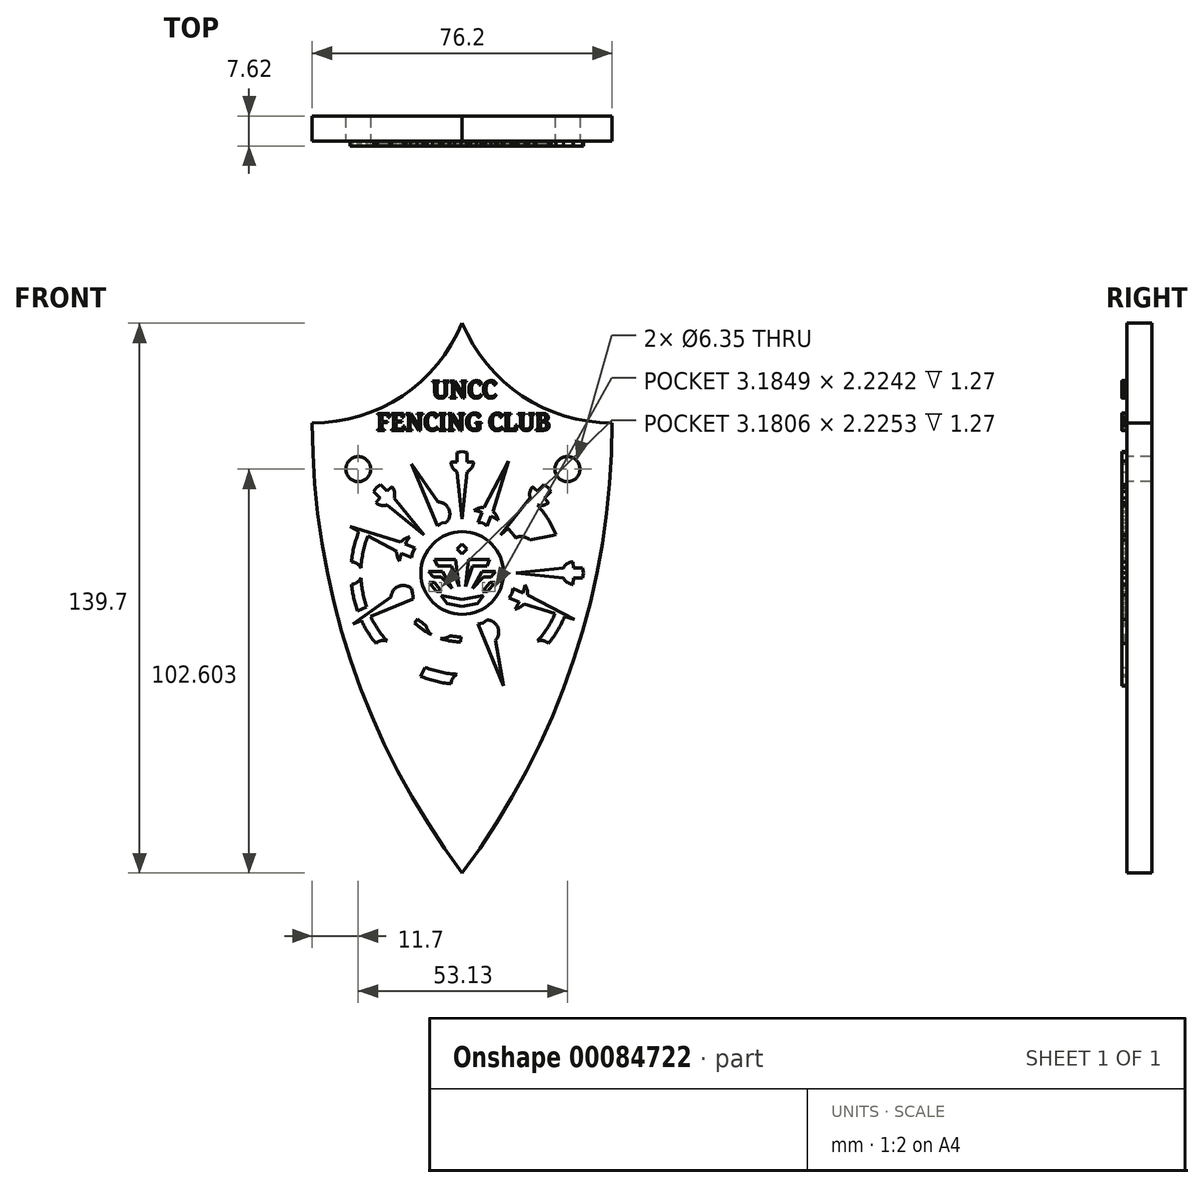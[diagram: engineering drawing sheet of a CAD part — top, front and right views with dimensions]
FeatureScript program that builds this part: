
annotation { "Feature Type Name" : "Feature", "Feature Type Description" : "" }
export const myFeature = defineFeature(function(context is Context, id is Id, definition is map)
    precondition{}
    {
        {
            var Q0;
            Q0=qCreatedBy(makeId("Front.planeOp"),FACE);
            var sketch = newSketch(context, id + "F0", { "sketchPlane" : qUnion([Q0])});
            skLineSegment(sketch, "E0", {"start": v(0, 0) * mm, "end": v(0, 38.1) * mm});
            skLineSegment(sketch, "E1", {"start": v(0, 38.1) * mm, "end": v(-38.1, 38.1) * mm});
            skLineSegment(sketch, "E2", {"start": v(0, 38.1) * mm, "end": v(0, 63.5) * mm});
            skLineSegment(sketch, "E3", {"start": v(0, 0) * mm, "end": v(0, -76.2) * mm});
            skArc(sketch, "E4", {"start": v(-38.1, 38.1) * mm, "mid": v(-28.32, -22.14) * mm, "end": v(0, -76.2) * mm});
            skArc(sketch, "E5", {"start": v(-38.1, 38.1) * mm, "mid": v(-15.2, 45.03) * mm, "end": v(0, 63.5) * mm});
            skArc(sketch, "E6.MirrorCS", {"start": v(38.1, 38.1) * mm, "mid": v(28.32, -22.14) * mm, "end": v(0, -76.2) * mm});
            skLineSegment(sketch, "E7.MirrorCS", {"start": v(0, 38.1) * mm, "end": v(38.1, 38.1) * mm});
            skArc(sketch, "E8.MirrorCS", {"start": v(38.1, 38.1) * mm, "mid": v(15.2, 45.03) * mm, "end": v(0, 63.5) * mm});
            skSolve(sketch);
        }
        {
            var Q0;
            Q0=makeQuery(id+"F0.imprint","IMPRINT",FACE,{"disambiguationData":[TD([[makeQuery(id+"F0.imprint","IMPRINT",EDGE,{"derivedFrom":sQuery(id+"F0.wireOp",EDGE,"E1")}),-1.0]])]});
            var Q1;
            Q1=makeQuery(id+"F0.imprint","IMPRINT",FACE,{"disambiguationData":[TD([[makeQuery(id+"F0.imprint","IMPRINT",EDGE,{"derivedFrom":sQuery(id+"F0.wireOp",EDGE,"E2")}),-1.0]])]});
            var Q2;
            Q2=makeQuery(id+"F0.imprint","IMPRINT",FACE,{"disambiguationData":[TD([[makeQuery(id+"F0.imprint","IMPRINT",EDGE,{"derivedFrom":sQuery(id+"F0.wireOp",EDGE,"E0")}),1.0]])]});
            var Q3;
            Q3=makeQuery(id+"F0.imprint","IMPRINT",FACE,{"disambiguationData":[TD([[makeQuery(id+"F0.imprint","IMPRINT",EDGE,{"derivedFrom":sQuery(id+"F0.wireOp",EDGE,"E0")}),-1.0]])]});
            extrude(context, id + "F1", {"entities" : qUnion([Q0, Q1, Q2, Q3]), "depth" : 6.35 * mm});
        }
        {
            var Q0;
            Q0=makeQuery(id+"F1.opExtrude","CAP_FACE",FACE,{"disambiguationData":[OSD([sQuery(id+"F0.wireOp",EDGE,"E4"),sQuery(id+"F0.wireOp",EDGE,"E5"),sQuery(id+"F0.wireOp",EDGE,"E6.MirrorCS"),sQuery(id+"F0.wireOp",EDGE,"E8.MirrorCS")])],"isStart":false});
            var sketch = newSketch(context, id + "F2", { "sketchPlane" : qUnion([Q0])});
            skCircle(sketch, "E9.cCircle", {"center": v(0, 0) * mm, "radius": 30.82 * mm, "construction": true});
            skLineSegment(sketch, "E9.0", {"start": v(30.82, 0) * mm, "end": v(28.48, -11.8) * mm});
            skLineSegment(sketch, "E9.1", {"start": v(28.48, -11.8) * mm, "end": v(21.8, -21.8) * mm});
            skLineSegment(sketch, "E9.2", {"start": v(21.8, -21.8) * mm, "end": v(11.8, -28.48) * mm});
            skLineSegment(sketch, "E9.3", {"start": v(11.8, -28.48) * mm, "end": v(0, -30.82) * mm});
            skLineSegment(sketch, "E9.4", {"start": v(0, -30.82) * mm, "end": v(-11.8, -28.48) * mm});
            skLineSegment(sketch, "E9.5", {"start": v(-11.8, -28.48) * mm, "end": v(-21.8, -21.8) * mm});
            skLineSegment(sketch, "E9.6", {"start": v(-21.8, -21.8) * mm, "end": v(-28.48, -11.8) * mm});
            skLineSegment(sketch, "E9.7", {"start": v(-28.48, -11.8) * mm, "end": v(-30.82, 0) * mm});
            skLineSegment(sketch, "E9.8", {"start": v(-30.82, 0) * mm, "end": v(-28.48, 11.8) * mm});
            skLineSegment(sketch, "E9.9", {"start": v(-28.48, 11.8) * mm, "end": v(-21.8, 21.8) * mm});
            skLineSegment(sketch, "E9.10", {"start": v(-21.8, 21.8) * mm, "end": v(-11.8, 28.48) * mm});
            skLineSegment(sketch, "E9.11", {"start": v(-11.8, 28.48) * mm, "end": v(0, 30.82) * mm});
            skLineSegment(sketch, "E9.12", {"start": v(0, 30.82) * mm, "end": v(11.8, 28.48) * mm});
            skLineSegment(sketch, "E9.13", {"start": v(11.8, 28.48) * mm, "end": v(21.8, 21.8) * mm});
            skLineSegment(sketch, "E9.14", {"start": v(21.8, 21.8) * mm, "end": v(28.48, 11.8) * mm});
            skLineSegment(sketch, "E9.15", {"start": v(28.48, 11.8) * mm, "end": v(30.82, 0) * mm});
            skCircle(sketch, "E10.cCircle", {"center": v(0, 0) * mm, "radius": 13.7 * mm, "construction": true});
            skLineSegment(sketch, "E10.0", {"start": v(13.7, 0) * mm, "end": v(12.66, -5.24) * mm});
            skLineSegment(sketch, "E10.1", {"start": v(12.66, -5.24) * mm, "end": v(9.69, -9.69) * mm});
            skLineSegment(sketch, "E10.2", {"start": v(9.69, -9.69) * mm, "end": v(5.24, -12.66) * mm});
            skLineSegment(sketch, "E10.3", {"start": v(5.24, -12.66) * mm, "end": v(0, -13.7) * mm});
            skLineSegment(sketch, "E10.4", {"start": v(0, -13.7) * mm, "end": v(-5.24, -12.66) * mm});
            skLineSegment(sketch, "E10.5", {"start": v(-5.24, -12.66) * mm, "end": v(-9.69, -9.69) * mm});
            skLineSegment(sketch, "E10.6", {"start": v(-9.69, -9.69) * mm, "end": v(-12.66, -5.24) * mm});
            skLineSegment(sketch, "E10.7", {"start": v(-12.66, -5.24) * mm, "end": v(-13.7, 0) * mm});
            skLineSegment(sketch, "E10.8", {"start": v(-13.7, 0) * mm, "end": v(-12.66, 5.24) * mm});
            skLineSegment(sketch, "E10.9", {"start": v(-12.66, 5.24) * mm, "end": v(-9.69, 9.69) * mm});
            skLineSegment(sketch, "E10.10", {"start": v(-9.69, 9.69) * mm, "end": v(-5.24, 12.66) * mm});
            skLineSegment(sketch, "E10.11", {"start": v(-5.24, 12.66) * mm, "end": v(0, 13.7) * mm});
            skLineSegment(sketch, "E10.12", {"start": v(0, 13.7) * mm, "end": v(5.24, 12.66) * mm});
            skLineSegment(sketch, "E10.13", {"start": v(5.24, 12.66) * mm, "end": v(9.69, 9.69) * mm});
            skLineSegment(sketch, "E10.14", {"start": v(9.69, 9.69) * mm, "end": v(12.66, 5.24) * mm});
            skLineSegment(sketch, "E10.15", {"start": v(12.66, 5.24) * mm, "end": v(13.7, 0) * mm});
            skLineSegment(sketch, "E11", {"start": v(-11.8, 28.48) * mm, "end": v(-9.5, 22.91) * mm});
            skLineSegment(sketch, "E12.MirrorCS", {"start": v(28.48, 11.8) * mm, "end": v(22.91, 9.5) * mm});
            skLineSegment(sketch, "E13.MirrorCS", {"start": v(-28.48, -11.8) * mm, "end": v(-22.91, -9.5) * mm});
            skLineSegment(sketch, "E14.MirrorCS", {"start": v(11.8, -28.48) * mm, "end": v(9.5, -22.91) * mm});
            skArc(sketch, "E15.0", {"start": v(-1.27, 25.71) * mm, "mid": v(-5.74, 25.1) * mm, "end": v(-10.04, 23.7) * mm});
            skArc(sketch, "E16.0", {"start": v(0, 17.5) * mm, "mid": v(-1.98, 17.4) * mm, "end": v(-3.94, 17.06) * mm});
            skArc(sketch, "E17.0", {"start": v(0, 16.24) * mm, "mid": v(-1.65, 16.16) * mm, "end": v(-3.28, 15.9) * mm});
            skArc(sketch, "E18.0", {"start": v(-1.27, 28.26) * mm, "mid": v(-6.51, 27.52) * mm, "end": v(-11.53, 25.83) * mm});
            skLineSegment(sketch, "E19.0", {"start": v(-1.27, 30.82) * mm, "end": v(-1.27, 28.26) * mm});
            skLineSegment(sketch, "E20.0", {"start": v(1.27, 30.82) * mm, "end": v(1.27, 28.26) * mm});
            skLineSegment(sketch, "E21", {"start": v(0, 13.7) * mm, "end": v(0.01, 25.74) * mm});
            skLineSegment(sketch, "E22.MirrorCS", {"start": v(0, -13.7) * mm, "end": v(-1.27, -25.71) * mm});
            skLineSegment(sketch, "E23.MirrorCS", {"start": v(0, -13.7) * mm, "end": v(1.27, -25.71) * mm});
            skArc(sketch, "E24.MirrorCS", {"start": v(-2.86, -28.14) * mm, "mid": v(-2.4, -26.7) * mm, "end": v(-1.27, -25.71) * mm});
            skArc(sketch, "E25.MirrorCS", {"start": v(1.27, -25.71) * mm, "mid": v(2.4, -26.7) * mm, "end": v(2.86, -28.14) * mm});
            skLineSegment(sketch, "E26.MirrorCS", {"start": v(1.27, -30.82) * mm, "end": v(1.27, -28.26) * mm});
            skLineSegment(sketch, "E27.MirrorCS", {"start": v(-1.27, -30.82) * mm, "end": v(-1.27, -28.26) * mm});
            skLineSegment(sketch, "E28.0", {"start": v(30.82, 1.27) * mm, "end": v(28.26, 1.27) * mm});
            skLineSegment(sketch, "E29.0", {"start": v(30.82, -1.27) * mm, "end": v(28.26, -1.27) * mm});
            skLineSegment(sketch, "E30", {"start": v(13.7, 0) * mm, "end": v(25.71, 1.27) * mm});
            skLineSegment(sketch, "E31", {"start": v(13.7, 0) * mm, "end": v(25.71, -1.27) * mm});
            skArc(sketch, "E32", {"start": v(28.14, 2.86) * mm, "mid": v(26.7, 2.4) * mm, "end": v(25.71, 1.27) * mm});
            skArc(sketch, "E33.trimOffspring", {"start": v(28.26, 1.27) * mm, "mid": v(27.74, 5.52) * mm, "end": v(26.6, 9.64) * mm});
            skArc(sketch, "E34.trimOffspring", {"start": v(25.71, 1.27) * mm, "mid": v(25.25, 5.02) * mm, "end": v(24.24, 8.67) * mm});
            skArc(sketch, "E35.trimOffspring", {"start": v(25.71, -1.27) * mm, "mid": v(26.7, -2.4) * mm, "end": v(28.14, -2.86) * mm});
            skArc(sketch, "E36.trimOffspring", {"start": v(16.24, 0.27) * mm, "mid": v(16.02, 2.67) * mm, "end": v(15.44, 5.02) * mm});
            skLineSegment(sketch, "E37.MirrorCS", {"start": v(-13.7, 0) * mm, "end": v(-25.71, 1.27) * mm});
            skLineSegment(sketch, "E38.MirrorCS", {"start": v(-13.7, 0) * mm, "end": v(-25.71, -1.27) * mm});
            skArc(sketch, "E39.MirrorCS", {"start": v(-28.14, 2.86) * mm, "mid": v(-26.7, 2.4) * mm, "end": v(-25.71, 1.27) * mm});
            skArc(sketch, "E40.MirrorCS", {"start": v(-25.71, -1.27) * mm, "mid": v(-26.7, -2.4) * mm, "end": v(-28.14, -2.86) * mm});
            skLineSegment(sketch, "E41.MirrorCS", {"start": v(-30.82, 1.27) * mm, "end": v(-28.26, 1.27) * mm});
            skLineSegment(sketch, "E42.MirrorCS", {"start": v(-30.82, -1.27) * mm, "end": v(-28.26, -1.27) * mm});
            skLineSegment(sketch, "E43.0", {"start": v(-22.7, 20.9) * mm, "end": v(-20.88, 19.08) * mm});
            skLineSegment(sketch, "E44.0", {"start": v(-20.9, 22.7) * mm, "end": v(-19.08, 20.88) * mm});
            skLineSegment(sketch, "E45.0", {"start": v(22.7, 20.9) * mm, "end": v(20.88, 19.08) * mm});
            skLineSegment(sketch, "E46.0", {"start": v(20.9, 22.7) * mm, "end": v(19.08, 20.88) * mm});
            skLineSegment(sketch, "E47", {"start": v(-19.08, 17.28) * mm, "end": v(-9.69, 9.69) * mm});
            skLineSegment(sketch, "E48", {"start": v(-9.69, 9.69) * mm, "end": v(-17.28, 19.08) * mm});
            skArc(sketch, "E49", {"start": v(-21.92, 17.87) * mm, "mid": v(-20.58, 17.2) * mm, "end": v(-19.08, 17.28) * mm});
            skLineSegment(sketch, "E50", {"start": v(17.28, 19.08) * mm, "end": v(9.69, 9.69) * mm});
            skLineSegment(sketch, "E51", {"start": v(9.69, 9.69) * mm, "end": v(19.08, 17.28) * mm});
            skArc(sketch, "E52", {"start": v(17.87, 21.92) * mm, "mid": v(17.2, 20.58) * mm, "end": v(17.28, 19.08) * mm});
            skArc(sketch, "E53.trimOffspring", {"start": v(-20.88, 19.08) * mm, "mid": v(-23.8, 15.28) * mm, "end": v(-26.04, 11.05) * mm});
            skArc(sketch, "E54.trimOffspring", {"start": v(19.08, 20.88) * mm, "mid": v(15.28, 23.8) * mm, "end": v(11.05, 26.04) * mm});
            skArc(sketch, "E55.trimOffspring", {"start": v(17.28, 19.08) * mm, "mid": v(13.97, 21.62) * mm, "end": v(10.3, 23.6) * mm});
            skArc(sketch, "E56.trimOffspring", {"start": v(19.08, 17.28) * mm, "mid": v(20.58, 17.2) * mm, "end": v(21.92, 17.87) * mm});
            skArc(sketch, "E57.trimOffspring", {"start": v(12.1, 12.66) * mm, "mid": v(10.09, 14.31) * mm, "end": v(7.86, 15.65) * mm});
            skArc(sketch, "E58.trimOffspring", {"start": v(-12.66, 12.1) * mm, "mid": v(-14.31, 10.09) * mm, "end": v(-15.65, 7.86) * mm});
            skArc(sketch, "E59.trimOffspring", {"start": v(-19.08, 17.28) * mm, "mid": v(-21.62, 13.97) * mm, "end": v(-23.6, 10.3) * mm});
            skArc(sketch, "E60.trimOffspring", {"start": v(-17.28, 19.08) * mm, "mid": v(-17.2, 20.58) * mm, "end": v(-17.87, 21.92) * mm});
            skArc(sketch, "E61.trimOffspring", {"start": v(-11.67, 11.3) * mm, "mid": v(-13.22, 9.43) * mm, "end": v(-14.47, 7.37) * mm});
            skArc(sketch, "E62.trimOffspring", {"start": v(11.3, 11.67) * mm, "mid": v(9.43, 13.22) * mm, "end": v(7.37, 14.47) * mm});
            skPoint(sketch, "E63.orphan", {"position": v(0, -30.82) * mm});
            skArc(sketch, "E64.trimOffspring", {"start": v(1.27, -28.26) * mm, "mid": v(5.52, -27.74) * mm, "end": v(9.64, -26.6) * mm});
            skArc(sketch, "E65.trimOffspring", {"start": v(1.27, -25.71) * mm, "mid": v(5.02, -25.25) * mm, "end": v(8.67, -24.24) * mm});
            skArc(sketch, "E66.trimOffspring", {"start": v(0.4, -17.5) * mm, "mid": v(2.99, -17.25) * mm, "end": v(5.5, -16.62) * mm});
            skArc(sketch, "E67.trimOffspring", {"start": v(0.27, -16.24) * mm, "mid": v(2.67, -16.02) * mm, "end": v(5.02, -15.44) * mm});
            skLineSegment(sketch, "E68.MirrorCS", {"start": v(-9.69, -9.69) * mm, "end": v(-17.28, -19.08) * mm});
            skLineSegment(sketch, "E69.MirrorCS", {"start": v(-19.08, -17.28) * mm, "end": v(-9.69, -9.69) * mm});
            skArc(sketch, "E70.MirrorCS", {"start": v(-21.92, -17.87) * mm, "mid": v(-20.58, -17.2) * mm, "end": v(-19.08, -17.28) * mm});
            skArc(sketch, "E71.MirrorCS", {"start": v(-17.28, -19.08) * mm, "mid": v(-17.2, -20.58) * mm, "end": v(-17.87, -21.92) * mm});
            skLineSegment(sketch, "E72.MirrorCS", {"start": v(-20.9, -22.7) * mm, "end": v(-19.08, -20.88) * mm});
            skLineSegment(sketch, "E73.MirrorCS", {"start": v(-22.7, -20.9) * mm, "end": v(-20.88, -19.08) * mm});
            skLineSegment(sketch, "E74.MirrorCS", {"start": v(17.28, -19.08) * mm, "end": v(9.69, -9.69) * mm});
            skLineSegment(sketch, "E75.MirrorCS", {"start": v(9.69, -9.69) * mm, "end": v(19.08, -17.28) * mm});
            skArc(sketch, "E76.MirrorCS", {"start": v(19.08, -17.28) * mm, "mid": v(20.58, -17.2) * mm, "end": v(21.92, -17.87) * mm});
            skArc(sketch, "E77.MirrorCS", {"start": v(17.87, -21.92) * mm, "mid": v(17.2, -20.58) * mm, "end": v(17.28, -19.08) * mm});
            skLineSegment(sketch, "E78.MirrorCS", {"start": v(20.9, -22.7) * mm, "end": v(19.08, -20.88) * mm});
            skLineSegment(sketch, "E79.MirrorCS", {"start": v(22.7, -20.9) * mm, "end": v(20.88, -19.08) * mm});
            skLineSegment(sketch, "E80", {"start": v(-28.48, 11.8) * mm, "end": v(-15.65, 7.86) * mm});
            skLineSegment(sketch, "E81", {"start": v(-28.48, 11.8) * mm, "end": v(-16.62, 5.5) * mm});
            skArc(sketch, "E82", {"start": v(-13.42, 9.14) * mm, "mid": v(-14.64, 8.68) * mm, "end": v(-15.65, 7.86) * mm});
            skArc(sketch, "E83.trimOffspring", {"start": v(-15.44, 5.02) * mm, "mid": v(-16.02, 2.67) * mm, "end": v(-16.24, 0.27) * mm});
            skArc(sketch, "E84.trimOffspring", {"start": v(-16.62, 5.5) * mm, "mid": v(-16.5, 4.21) * mm, "end": v(-15.95, 3.03) * mm});
            skArc(sketch, "E85.trimOffspring", {"start": v(-16.62, 5.5) * mm, "mid": v(-17.25, 2.99) * mm, "end": v(-17.5, 0.4) * mm});
            skLineSegment(sketch, "E86.trimOffspring", {"start": v(-14.47, 7.37) * mm, "end": v(-11.94, 6.32) * mm});
            skLineSegment(sketch, "E87.trimOffspring", {"start": v(-15.44, 5.02) * mm, "end": v(-12.9, 3.97) * mm});
            skLineSegment(sketch, "E88", {"start": v(5.5, 16.62) * mm, "end": v(11.8, 28.48) * mm});
            skLineSegment(sketch, "E89", {"start": v(11.8, 28.48) * mm, "end": v(7.86, 15.65) * mm});
            skArc(sketch, "E90.trimOffspring", {"start": v(9.14, 13.42) * mm, "mid": v(8.68, 14.64) * mm, "end": v(7.86, 15.65) * mm});
            skLineSegment(sketch, "E91.trimOffspring", {"start": v(5.02, 15.44) * mm, "end": v(3.97, 12.9) * mm});
            skArc(sketch, "E92.trimOffspring", {"start": v(5.02, 15.44) * mm, "mid": v(2.54, 16.04) * mm, "end": v(0, 16.24) * mm});
            skLineSegment(sketch, "E93.trimOffspring", {"start": v(7.37, 14.47) * mm, "end": v(6.32, 11.94) * mm});
            skArc(sketch, "E94.trimOffspring", {"start": v(5.5, 16.62) * mm, "mid": v(4.21, 16.5) * mm, "end": v(3.03, 15.95) * mm});
            skArc(sketch, "E95.trimOffspring", {"start": v(5.5, 16.62) * mm, "mid": v(2.8, 17.29) * mm, "end": v(0, 17.5) * mm});
            skArc(sketch, "E96.MirrorCS", {"start": v(-7.86, -15.65) * mm, "mid": v(-8.68, -14.64) * mm, "end": v(-9.14, -13.42) * mm});
            skArc(sketch, "E97.MirrorCS", {"start": v(-3.03, -15.95) * mm, "mid": v(-4.21, -16.5) * mm, "end": v(-5.5, -16.62) * mm});
            skLineSegment(sketch, "E98.MirrorCS", {"start": v(-7.86, -15.65) * mm, "end": v(-11.8, -28.48) * mm});
            skLineSegment(sketch, "E99.MirrorCS", {"start": v(-11.8, -28.48) * mm, "end": v(-5.5, -16.62) * mm});
            skLineSegment(sketch, "E100.MirrorCS", {"start": v(-7.37, -14.47) * mm, "end": v(-6.32, -11.94) * mm});
            skLineSegment(sketch, "E101.MirrorCS", {"start": v(-5.02, -15.44) * mm, "end": v(-3.97, -12.9) * mm});
            skArc(sketch, "E102.trimOffspring", {"start": v(-5.02, -15.44) * mm, "mid": v(-2.67, -16.02) * mm, "end": v(-0.27, -16.24) * mm});
            skArc(sketch, "E103.trimOffspring", {"start": v(-5.5, -16.62) * mm, "mid": v(-2.99, -17.25) * mm, "end": v(-0.4, -17.5) * mm});
            skArc(sketch, "E104.trimOffspring", {"start": v(16.62, -5.5) * mm, "mid": v(17.25, -2.99) * mm, "end": v(17.5, -0.4) * mm});
            skArc(sketch, "E105.trimOffspring", {"start": v(15.44, -5.02) * mm, "mid": v(16.02, -2.67) * mm, "end": v(16.24, -0.27) * mm});
            skArc(sketch, "E106.trimOffspring", {"start": v(-28.26, -1.27) * mm, "mid": v(-27.52, -6.51) * mm, "end": v(-25.83, -11.53) * mm});
            skArc(sketch, "E107.trimOffspring", {"start": v(-25.71, -1.27) * mm, "mid": v(-25.1, -5.74) * mm, "end": v(-23.7, -10.04) * mm});
            skArc(sketch, "E108.trimOffspring", {"start": v(-17.5, -0.4) * mm, "mid": v(-17.37, -2.18) * mm, "end": v(-17.06, -3.94) * mm});
            skArc(sketch, "E109.trimOffspring", {"start": v(-19.08, -20.88) * mm, "mid": v(-15.28, -23.8) * mm, "end": v(-11.05, -26.04) * mm});
            skArc(sketch, "E110.trimOffspring", {"start": v(-17.28, -19.08) * mm, "mid": v(-13.97, -21.62) * mm, "end": v(-10.3, -23.6) * mm});
            skArc(sketch, "E111.trimOffspring", {"start": v(-12.1, -12.66) * mm, "mid": v(-10.09, -14.31) * mm, "end": v(-7.86, -15.65) * mm});
            skArc(sketch, "E112.trimOffspring", {"start": v(11.67, -11.3) * mm, "mid": v(13.22, -9.43) * mm, "end": v(14.47, -7.37) * mm});
            skArc(sketch, "E113.trimOffspring", {"start": v(12.66, -12.1) * mm, "mid": v(14.31, -10.09) * mm, "end": v(15.65, -7.86) * mm});
            skArc(sketch, "E114.trimOffspring", {"start": v(19.08, -17.28) * mm, "mid": v(21.62, -13.97) * mm, "end": v(23.6, -10.3) * mm});
            skArc(sketch, "E115.trimOffspring", {"start": v(20.88, -19.08) * mm, "mid": v(23.8, -15.28) * mm, "end": v(26.04, -11.05) * mm});
            skArc(sketch, "E116.trimOffspring", {"start": v(9.4, 23.97) * mm, "mid": v(5.4, 25.17) * mm, "end": v(1.27, 25.71) * mm});
            skArc(sketch, "E117.trimOffspring", {"start": v(10.6, 26.22) * mm, "mid": v(6.02, 27.64) * mm, "end": v(1.27, 28.26) * mm});
            skArc(sketch, "E118.trimOffspring", {"start": v(-26.22, 10.6) * mm, "mid": v(-27.64, 6.02) * mm, "end": v(-28.26, 1.27) * mm});
            skArc(sketch, "E119.trimOffspring", {"start": v(-23.97, 9.4) * mm, "mid": v(-25.17, 5.4) * mm, "end": v(-25.71, 1.27) * mm});
            skArc(sketch, "E120.trimOffspring", {"start": v(-11.3, -11.67) * mm, "mid": v(-9.43, -13.22) * mm, "end": v(-7.37, -14.47) * mm});
            skArc(sketch, "E121.trimOffspring", {"start": v(-16.24, -0.27) * mm, "mid": v(-16.14, -1.78) * mm, "end": v(-15.9, -3.28) * mm});
            skArc(sketch, "E122.trimOffspring", {"start": v(26.22, -10.6) * mm, "mid": v(27.64, -6.02) * mm, "end": v(28.26, -1.27) * mm});
            skArc(sketch, "E123.trimOffspring", {"start": v(23.97, -9.4) * mm, "mid": v(25.17, -5.4) * mm, "end": v(25.71, -1.27) * mm});
            skArc(sketch, "E124.trimOffspring", {"start": v(-10.6, -26.22) * mm, "mid": v(-6.02, -27.64) * mm, "end": v(-1.27, -28.26) * mm});
            skArc(sketch, "E125.trimOffspring", {"start": v(-9.4, -23.97) * mm, "mid": v(-5.4, -25.17) * mm, "end": v(-1.27, -25.71) * mm});
            skPoint(sketch, "E126.endSnap1", {"position": v(-11.17, -7.46) * mm});
            skLineSegment(sketch, "E127", {"start": v(-5.24, -4.65) * mm, "end": v(-6.51, -4.65) * mm});
            skLineSegment(sketch, "E128", {"start": v(-6.51, -4.65) * mm, "end": v(-8.42, -2.42) * mm});
            skLineSegment(sketch, "E129", {"start": v(-7.08, -2.42) * mm, "end": v(-5.24, -4.65) * mm});
            skLineSegment(sketch, "E130", {"start": v(-2.6, -3.96) * mm, "end": v(-5.38, -1.02) * mm});
            skLineSegment(sketch, "E131", {"start": v(-5.38, -1.02) * mm, "end": v(-7.31, -1.02) * mm});
            skLineSegment(sketch, "E132", {"start": v(-7.31, -1.02) * mm, "end": v(-8.5, 0.44) * mm});
            skLineSegment(sketch, "E133", {"start": v(-8.5, 0.44) * mm, "end": v(-5.03, 0.44) * mm});
            skLineSegment(sketch, "E134", {"start": v(-5.03, 0.44) * mm, "end": v(-2.6, -3.96) * mm});
            skLineSegment(sketch, "E135", {"start": v(-0.82, -3.38) * mm, "end": v(-2.68, 1.76) * mm});
            skLineSegment(sketch, "E136", {"start": v(-2.68, 1.76) * mm, "end": v(-6.3, 1.76) * mm});
            skLineSegment(sketch, "E137", {"start": v(-6.3, 1.76) * mm, "end": v(-7.01, 3.5) * mm});
            skLineSegment(sketch, "E138", {"start": v(-7.01, 3.5) * mm, "end": v(-1.66, 3.5) * mm});
            skLineSegment(sketch, "E139", {"start": v(-1.66, 3.5) * mm, "end": v(-0.82, -3.38) * mm});
            skLineSegment(sketch, "E140", {"start": v(-8.42, -2.42) * mm, "end": v(-7.08, -2.42) * mm});
            skLineSegment(sketch, "E141", {"start": v(0, 7.36) * mm, "end": v(-1.27, 6.1) * mm});
            skLineSegment(sketch, "E142", {"start": v(-1.27, 6.1) * mm, "end": v(0, 4.82) * mm});
            skLineSegment(sketch, "E143", {"start": v(0, 4.82) * mm, "end": v(0, 7.36) * mm});
            skLineSegment(sketch, "E144", {"start": v(-5.42, -5.68) * mm, "end": v(-3.9, -7.76) * mm});
            skLineSegment(sketch, "E145", {"start": v(-3.9, -7.76) * mm, "end": v(0, -8.45) * mm});
            skLineSegment(sketch, "E146", {"start": v(0, -8.45) * mm, "end": v(0, -6.75) * mm});
            skLineSegment(sketch, "E147", {"start": v(0, -6.75) * mm, "end": v(-5.42, -5.68) * mm});
            skLineSegment(sketch, "E148.MirrorCS", {"start": v(5.38, -5.7) * mm, "end": v(3.85, -7.77) * mm});
            skLineSegment(sketch, "E149.MirrorCS", {"start": v(7.28, -1.03) * mm, "end": v(8.47, 0.42) * mm});
            skLineSegment(sketch, "E150.MirrorCS", {"start": v(8.47, 0.42) * mm, "end": v(5, 0.43) * mm});
            skLineSegment(sketch, "E151.MirrorCS", {"start": v(7.04, -2.44) * mm, "end": v(5.2, -4.66) * mm});
            skLineSegment(sketch, "E152.MirrorCS", {"start": v(2.56, -3.96) * mm, "end": v(5.35, -1.03) * mm});
            skLineSegment(sketch, "E153.MirrorCS", {"start": v(5, 0.43) * mm, "end": v(2.56, -3.96) * mm});
            skLineSegment(sketch, "E154.MirrorCS", {"start": v(-0.04, -6.75) * mm, "end": v(5.38, -5.7) * mm});
            skLineSegment(sketch, "E155.MirrorCS", {"start": v(7, 3.5) * mm, "end": v(1.64, 3.5) * mm});
            skLineSegment(sketch, "E156.MirrorCS", {"start": v(5.35, -1.03) * mm, "end": v(7.28, -1.03) * mm});
            skLineSegment(sketch, "E157.MirrorCS", {"start": v(1.26, 6.09) * mm, "end": v(-0.02, 4.82) * mm});
            skLineSegment(sketch, "E158.MirrorCS", {"start": v(1.64, 3.5) * mm, "end": v(0.79, -3.38) * mm});
            skLineSegment(sketch, "E159.MirrorCS", {"start": v(6.48, -4.66) * mm, "end": v(8.4, -2.44) * mm});
            skLineSegment(sketch, "E160.MirrorCS", {"start": v(0.79, -3.38) * mm, "end": v(2.66, 1.75) * mm});
            skLineSegment(sketch, "E161.MirrorCS", {"start": v(3.85, -7.77) * mm, "end": v(-0.04, -8.45) * mm});
            skLineSegment(sketch, "E162.MirrorCS", {"start": v(0, 7.36) * mm, "end": v(1.26, 6.09) * mm});
            skLineSegment(sketch, "E163.MirrorCS", {"start": v(-0.02, 4.82) * mm, "end": v(0, 7.36) * mm});
            skLineSegment(sketch, "E164.MirrorCS", {"start": v(5.2, -4.66) * mm, "end": v(6.48, -4.66) * mm});
            skLineSegment(sketch, "E165.MirrorCS", {"start": v(6.28, 1.75) * mm, "end": v(7, 3.5) * mm});
            skLineSegment(sketch, "E166.MirrorCS", {"start": v(2.66, 1.75) * mm, "end": v(6.28, 1.75) * mm});
            skLineSegment(sketch, "E167.MirrorCS", {"start": v(8.4, -2.44) * mm, "end": v(7.04, -2.44) * mm});
            skLineSegment(sketch, "E168.MirrorCS", {"start": v(-0.04, -8.45) * mm, "end": v(-0.04, -6.75) * mm});
            skCircle(sketch, "E169", {"center": v(0, 0) * mm, "radius": 10.5 * mm});
            skLineSegment(sketch, "E170", {"start": v(-11.8, -28.48) * mm, "end": v(-5.24, -12.66) * mm});
            skLineSegment(sketch, "E171.MirrorCS", {"start": v(14.47, -7.37) * mm, "end": v(11.94, -6.32) * mm});
            skLineSegment(sketch, "E172.MirrorCS", {"start": v(15.44, -5.02) * mm, "end": v(12.9, -3.97) * mm});
            skArc(sketch, "E173.MirrorCS", {"start": v(15.95, -3.03) * mm, "mid": v(16.5, -4.21) * mm, "end": v(16.62, -5.5) * mm});
            skArc(sketch, "E174.MirrorCS", {"start": v(15.65, -7.86) * mm, "mid": v(14.64, -8.68) * mm, "end": v(13.42, -9.14) * mm});
            skLineSegment(sketch, "E175.MirrorCS", {"start": v(28.48, -11.8) * mm, "end": v(15.65, -7.86) * mm});
            skLineSegment(sketch, "E176.MirrorCS", {"start": v(28.48, -11.8) * mm, "end": v(16.62, -5.5) * mm});
            skLineSegment(sketch, "E177", {"start": v(-30.82, 0) * mm, "end": v(-13.7, 0) * mm});
            skLineSegment(sketch, "E178.MirrorCS", {"start": v(0, 13.7) * mm, "end": v(-1.27, 25.71) * mm});
            skLineSegment(sketch, "E179.MirrorCS", {"start": v(0, 13.7) * mm, "end": v(1.27, 25.71) * mm});
            skArc(sketch, "E180", {"start": v(-2.86, 28.14) * mm, "mid": v(-2.4, 26.7) * mm, "end": v(-1.27, 25.71) * mm});
            skArc(sketch, "E181.trimOffspring", {"start": v(1.27, 25.71) * mm, "mid": v(2.4, 26.7) * mm, "end": v(2.86, 28.14) * mm});
            skLineSegment(sketch, "E182.0", {"start": v(12.97, -28) * mm, "end": v(8.46, -17.1) * mm});
            skLineSegment(sketch, "E183.0", {"start": v(10.62, -28.96) * mm, "end": v(3.97, -12.9) * mm});
            skLineSegment(sketch, "E184.0", {"start": v(-28, -12.97) * mm, "end": v(-11.94, -6.32) * mm});
            skLineSegment(sketch, "E185.0", {"start": v(-28.96, -10.62) * mm, "end": v(-18.07, -6.11) * mm});
            skPoint(sketch, "E186", {"position": v(5.5, -16.62) * mm});
            skPoint(sketch, "E187", {"position": v(-15.65, -7.86) * mm});
            skArc(sketch, "E188", {"start": v(8.46, -17.1) * mm, "mid": v(9.05, -13.83) * mm, "end": v(6.32, -11.94) * mm});
            skArc(sketch, "E189", {"start": v(-17.1, -8.46) * mm, "mid": v(-13.83, -9.05) * mm, "end": v(-11.94, -6.32) * mm});
            skArc(sketch, "E190", {"start": v(-16.55, -8.23) * mm, "mid": v(-13.46, -8.23) * mm, "end": v(-12.66, -5.24) * mm});
            skLineSegment(sketch, "E191", {"start": v(10.53, -28.73) * mm, "end": v(8.46, -17.1) * mm});
            skLineSegment(sketch, "E192", {"start": v(-27.76, -12.87) * mm, "end": v(-18.07, -6.11) * mm});
            skArc(sketch, "E193.trimOffspring", {"start": v(4.2, -13.46) * mm, "mid": v(3.87, -15.98) * mm, "end": v(5.88, -17.52) * mm});
            skArc(sketch, "E194.trimOffspring", {"start": v(3.97, -12.9) * mm, "mid": v(3.38, -16.18) * mm, "end": v(6.11, -18.07) * mm});
            skArc(sketch, "E195.trimOffspring", {"start": v(9.28, -14.85) * mm, "mid": v(10.74, -13.83) * mm, "end": v(12.1, -12.66) * mm});
            skArc(sketch, "E196.trimOffspring", {"start": v(8.93, -13.57) * mm, "mid": v(10.15, -12.67) * mm, "end": v(11.3, -11.67) * mm});
            skLineSegment(sketch, "E197.trimOffspring", {"start": v(6.4, -12.12) * mm, "end": v(6.32, -11.94) * mm});
            skArc(sketch, "E198.trimOffspring", {"start": v(9.66, -23.86) * mm, "mid": v(13.68, -21.8) * mm, "end": v(17.28, -19.08) * mm});
            skArc(sketch, "E199.trimOffspring", {"start": v(10.11, -26.41) * mm, "mid": v(14.86, -24.07) * mm, "end": v(19.08, -20.88) * mm});
            skLineSegment(sketch, "E200.trimOffspring", {"start": v(-13.09, -4.05) * mm, "end": v(-12.9, -3.97) * mm});
            skArc(sketch, "E201.trimOffspring", {"start": v(-15.65, -7.86) * mm, "mid": v(-14.31, -10.09) * mm, "end": v(-12.66, -12.1) * mm});
            skArc(sketch, "E202.trimOffspring", {"start": v(-14.47, -7.37) * mm, "mid": v(-13.22, -9.43) * mm, "end": v(-11.67, -11.3) * mm});
            skArc(sketch, "E203.trimOffspring", {"start": v(-25.62, -11.99) * mm, "mid": v(-23.52, -15.71) * mm, "end": v(-20.88, -19.08) * mm});
            skArc(sketch, "E204.trimOffspring", {"start": v(-23.27, -11.01) * mm, "mid": v(-21.4, -14.3) * mm, "end": v(-19.08, -17.28) * mm});
            skArc(sketch, "E205.trimOffspring", {"start": v(-12.9, -3.97) * mm, "mid": v(-16.18, -3.38) * mm, "end": v(-18.07, -6.11) * mm});
            skArc(sketch, "E206.MirrorCS", {"start": v(-6.11, 18.07) * mm, "mid": v(-3.38, 16.18) * mm, "end": v(-3.97, 12.9) * mm});
            skLineSegment(sketch, "E207.MirrorCS", {"start": v(-12.97, 28) * mm, "end": v(-6.32, 11.94) * mm});
            skLineSegment(sketch, "E208.MirrorCS", {"start": v(-12.87, 27.76) * mm, "end": v(-6.11, 18.07) * mm});
            skLineSegment(sketch, "E209.MirrorCS", {"start": v(28.73, 10.53) * mm, "end": v(17.1, 8.46) * mm});
            skLineSegment(sketch, "E210.MirrorCS", {"start": v(28.96, 10.62) * mm, "end": v(12.9, 3.97) * mm});
            skArc(sketch, "E211.MirrorCS", {"start": v(11.94, 6.32) * mm, "mid": v(13.83, 9.05) * mm, "end": v(17.1, 8.46) * mm});
            skArc(sketch, "E212.trimOffspring", {"start": v(13.57, 8.93) * mm, "mid": v(12.67, 10.15) * mm, "end": v(11.67, 11.3) * mm});
            skArc(sketch, "E213.trimOffspring", {"start": v(14.85, 9.28) * mm, "mid": v(14.06, 10.43) * mm, "end": v(13.2, 11.52) * mm});
            skArc(sketch, "E214.trimOffspring", {"start": v(23.86, 9.66) * mm, "mid": v(21.8, 13.68) * mm, "end": v(19.08, 17.28) * mm});
            skArc(sketch, "E215.trimOffspring", {"start": v(26.41, 10.11) * mm, "mid": v(24.07, 14.86) * mm, "end": v(20.88, 19.08) * mm});
            skArc(sketch, "E216.trimOffspring", {"start": v(-7.86, 15.65) * mm, "mid": v(-10.09, 14.31) * mm, "end": v(-12.1, 12.66) * mm});
            skArc(sketch, "E217.trimOffspring", {"start": v(-7.37, 14.47) * mm, "mid": v(-9.43, 13.22) * mm, "end": v(-11.3, 11.67) * mm});
            skArc(sketch, "E218.trimOffspring", {"start": v(-11.99, 25.62) * mm, "mid": v(-15.71, 23.52) * mm, "end": v(-19.08, 20.88) * mm});
            skArc(sketch, "E219.trimOffspring", {"start": v(-11.01, 23.27) * mm, "mid": v(-14.3, 21.4) * mm, "end": v(-17.28, 19.08) * mm});
            skPoint(sketch, "E220.orphan", {"position": v(12.49, 6.55) * mm});
            skPoint(sketch, "E221.orphan", {"position": v(12.92, 6.29) * mm});
            skPoint(sketch, "E222.trimOffspring.end.orphan", {"position": v(-17.52, -5.88) * mm});
            skPoint(sketch, "E222.trimOffspring.start.orphan", {"position": v(-13.46, -4.2) * mm});
            skPoint(sketch, "E223.end.orphan", {"position": v(6.55, -12.49) * mm});
            skPoint(sketch, "E223.start.orphan", {"position": v(8.23, -16.55) * mm});
            skPoint(sketch, "E224.orphan", {"position": v(-4.2, 13.46) * mm});
            skPoint(sketch, "E225.orphan", {"position": v(-5.88, 17.52) * mm});
            skSolve(sketch);
        }
        {
            var Q0;
            {var subQ0=sQuery(id+"F2.wireOp",EDGE,"UNDyexvm-xnox-bElG-6aDN-hg5ER65SXjyc");Q0=makeQuery(id+"F2.imprint","IMPRINT",FACE,{"disambiguationData":[TD([[makeQuery(id+"F2.imprint","IMPRINT",EDGE,{"derivedFrom":subQ0}),1.0]])]});}
            var Q1;
            {var subQ0=sQuery(id+"F2.wireOp",EDGE,"E90.trimOffspring");Q1=makeQuery(id+"F2.imprint","IMPRINT",FACE,{"disambiguationData":[TD([[makeQuery(id+"F2.imprint","IMPRINT",EDGE,{"derivedFrom":subQ0}),1.0]])]});}
            var Q2;
            {var subQ18=sQuery(id+"F2.wireOp",EDGE,"E49");Q2=makeQuery(id+"F2.imprint","IMPRINT",FACE,{"disambiguationData":[TD([[makeQuery(id+"F2.imprint","IMPRINT",EDGE,{"derivedFrom":subQ18}),1.0]])]});}
            var Q3;
            {var subQ7=sQuery(id+"F2.wireOp",EDGE,"E82");Q3=makeQuery(id+"F2.imprint","IMPRINT",FACE,{"disambiguationData":[TD([[makeQuery(id+"F2.imprint","IMPRINT",EDGE,{"derivedFrom":subQ7}),1.0]])]});}
            var Q4;
            {var subQ6=sQuery(id+"F2.wireOp",EDGE,"E39.MirrorCS");Q4=makeQuery(id+"F2.imprint","IMPRINT",FACE,{"disambiguationData":[TD([[makeQuery(id+"F2.imprint","IMPRINT",EDGE,{"derivedFrom":subQ6}),-1.0]])]});}
            var Q5;
            {var subQ0=sQuery(id+"F2.wireOp",EDGE,"E70.MirrorCS");Q5=makeQuery(id+"F2.imprint","IMPRINT",FACE,{"disambiguationData":[TD([[makeQuery(id+"F2.imprint","IMPRINT",EDGE,{"derivedFrom":subQ0}),-1.0]])]});}
            var Q6;
            {var subQ9=sQuery(id+"F2.wireOp",EDGE,"E96.MirrorCS");Q6=makeQuery(id+"F2.imprint","IMPRINT",FACE,{"disambiguationData":[TD([[makeQuery(id+"F2.imprint","IMPRINT",EDGE,{"derivedFrom":subQ9}),-1.0]])]});}
            var Q7;
            {var subQ6=sQuery(id+"F2.wireOp",EDGE,"E24.MirrorCS");Q7=makeQuery(id+"F2.imprint","IMPRINT",FACE,{"disambiguationData":[TD([[makeQuery(id+"F2.imprint","IMPRINT",EDGE,{"derivedFrom":subQ6}),-1.0]])]});}
            var Q8;
            {var subQ0=sQuery(id+"F2.wireOp",EDGE,"E76.MirrorCS");Q8=makeQuery(id+"F2.imprint","IMPRINT",FACE,{"disambiguationData":[TD([[makeQuery(id+"F2.imprint","IMPRINT",EDGE,{"derivedFrom":subQ0}),-1.0]])]});}
            var Q9;
            {var subQ0=sQuery(id+"F2.wireOp",EDGE,"27fd897c-9a95-4cc9-a76d-b57b807ea3900.MirrorCS");Q9=makeQuery(id+"F2.imprint","IMPRINT",FACE,{"disambiguationData":[TD([[makeQuery(id+"F2.imprint","IMPRINT",EDGE,{"derivedFrom":subQ0}),-1.0]])]});}
            var Q10;
            {var subQ13=sQuery(id+"F2.wireOp",EDGE,"E32");Q10=makeQuery(id+"F2.imprint","IMPRINT",FACE,{"disambiguationData":[TD([[makeQuery(id+"F2.imprint","IMPRINT",EDGE,{"derivedFrom":subQ13}),1.0]])]});}
            var Q11;
            {var subQ18=sQuery(id+"F2.wireOp",EDGE,"E52");Q11=makeQuery(id+"F2.imprint","IMPRINT",FACE,{"disambiguationData":[TD([[makeQuery(id+"F2.imprint","IMPRINT",EDGE,{"derivedFrom":subQ18}),1.0]])]});}
            var Q12;
            {var subQ0=sQuery(id+"F2.wireOp",EDGE,"E40.MirrorCS");Q12=makeQuery(id+"F2.imprint","IMPRINT",FACE,{"disambiguationData":[TD([[makeQuery(id+"F2.imprint","IMPRINT",EDGE,{"derivedFrom":subQ0}),-1.0]])]});}
            var Q13;
            {var subQ17=sQuery(id+"F2.wireOp",EDGE,"E180");Q13=makeQuery(id+"F2.imprint","IMPRINT",FACE,{"disambiguationData":[TD([[makeQuery(id+"F2.imprint","IMPRINT",EDGE,{"derivedFrom":subQ17}),1.0]])]});}
            var Q14;
            {var subQ8=sQuery(id+"F2.wireOp",EDGE,"E171.MirrorCS");Q14=makeQuery(id+"F2.imprint","IMPRINT",FACE,{"disambiguationData":[TD([[makeQuery(id+"F2.imprint","IMPRINT",EDGE,{"derivedFrom":subQ8}),-1.0]])]});}
            var Q15;
            {var subQ4=sQuery(id+"F2.wireOp",EDGE,"E97.MirrorCS");Q15=makeQuery(id+"F2.imprint","IMPRINT",FACE,{"disambiguationData":[TD([[makeQuery(id+"F2.imprint","IMPRINT",EDGE,{"derivedFrom":subQ4}),-1.0]])]});}
            var Q16;
            {var subQ3=sQuery(id+"F2.wireOp",EDGE,"E92.trimOffspring");var subQ5=sQuery(id+"F2.wireOp",EDGE,"E179.MirrorCS");var subQ6=makeQuery(id+"F2.imprint","INTERSECT",VERTEX,{"derivedFrom":[subQ3,subQ5]});Q16=makeQuery(id+"F2.imprint","IMPRINT",FACE,{"disambiguationData":[TD([[makeQuery(id+"F2.imprint","IMPRINT",EDGE,{"disambiguationData":[TD([[subQ6,-1.0]])],"derivedFrom":subQ5}),1.0]])]});}
            var Q17;
            {var subQ1=sQuery(id+"F2.wireOp",EDGE,"E16.0");var subQ3=sQuery(id+"F2.wireOp",EDGE,"E178.MirrorCS");var subQ4=makeQuery(id+"F2.imprint","INTERSECT",VERTEX,{"derivedFrom":[subQ1,subQ3]});Q17=makeQuery(id+"F2.imprint","IMPRINT",FACE,{"disambiguationData":[TD([[makeQuery(id+"F2.imprint","IMPRINT",EDGE,{"disambiguationData":[TD([[subQ4,1.0]])],"derivedFrom":subQ3}),-1.0]])]});}
            var Q18;
            {var subQ1=sQuery(id+"F2.wireOp",EDGE,"E17.0");var subQ3=sQuery(id+"F2.wireOp",EDGE,"E178.MirrorCS");var subQ4=makeQuery(id+"F2.imprint","INTERSECT",VERTEX,{"derivedFrom":[subQ1,subQ3]});Q18=makeQuery(id+"F2.imprint","IMPRINT",FACE,{"disambiguationData":[TD([[makeQuery(id+"F2.imprint","IMPRINT",EDGE,{"disambiguationData":[TD([[subQ4,1.0]])],"derivedFrom":subQ1}),1.0]])]});}
            var Q19;
            {var subQ0=sQuery(id+"F2.wireOp",EDGE,"E179.MirrorCS");var subQ3=sQuery(id+"F2.wireOp",EDGE,"E92.trimOffspring");var subQ5=makeQuery(id+"F2.imprint","INTERSECT",VERTEX,{"derivedFrom":[subQ3,subQ0]});Q19=makeQuery(id+"F2.imprint","IMPRINT",FACE,{"disambiguationData":[TD([[makeQuery(id+"F2.imprint","IMPRINT",EDGE,{"disambiguationData":[TD([[subQ5,-1.0]])],"derivedFrom":subQ3}),1.0]])]});}
            var Q20;
            {var subQ13=sQuery(id+"F2.wireOp",EDGE,"E10.11");var subQ15=sQuery(id+"F2.wireOp",EDGE,"E10.10");var subQ16=makeQuery(id+"F2.imprint","INTERSECT",VERTEX,{"derivedFrom":[subQ15,subQ13]});Q20=makeQuery(id+"F2.imprint","IMPRINT",FACE,{"disambiguationData":[TD([[makeQuery(id+"F2.imprint","IMPRINT",EDGE,{"disambiguationData":[TD([[subQ16,1.0]])],"derivedFrom":subQ15}),1.0]])]});}
            var Q21;
            Q21=makeQuery(id+"F2.imprint","IMPRINT",FACE,{"disambiguationData":[TD([[makeQuery(id+"F2.imprint","IMPRINT",EDGE,{"derivedFrom":sQuery(id+"F2.wireOp",EDGE,"E223")}),-1.0]])]});
            var Q22;
            {var subQ8=sQuery(id+"F2.wireOp",EDGE,"E211.MirrorCS");var subQ10=makeQuery(id+"F2.imprint","IMPRINT",VERTEX,{"derivedFrom":subQ8});Q22=makeQuery(id+"F2.imprint","IMPRINT",FACE,{"disambiguationData":[TD([[makeQuery(id+"F2.imprint","IMPRINT",EDGE,{"disambiguationData":[TD([[subQ10,1.0]])],"derivedFrom":subQ8}),-1.0]])]});}
            var Q23;
            {var subQ3=sQuery(id+"F2.wireOp",EDGE,"E184.0");var subQ17=makeQuery(id+"F2.imprint","INTERSECT",VERTEX,{"derivedFrom":[subQ3,sQuery(id+"F2.wireOp",EDGE,"E203.trimOffspring")]});Q23=makeQuery(id+"F2.imprint","IMPRINT",FACE,{"disambiguationData":[TD([[makeQuery(id+"F2.imprint","IMPRINT",EDGE,{"disambiguationData":[TD([[subQ17,-1.0]])],"derivedFrom":subQ3}),1.0]])]});}
            var Q24;
            {var subQ18=sQuery(id+"F2.wireOp",EDGE,"23f5d9e5-fa4a-421b-99c0-b9a638da6357.trimOffspring");Q24=makeQuery(id+"F2.imprint","IMPRINT",FACE,{"disambiguationData":[TD([[makeQuery(id+"F2.imprint","IMPRINT",EDGE,{"derivedFrom":subQ18}),1.0]])]});}
            var Q25;
            {var subQ2=sQuery(id+"F2.wireOp",EDGE,"E10.3");var subQ17=sQuery(id+"F2.wireOp",EDGE,"E10.2");var subQ18=makeQuery(id+"F2.imprint","INTERSECT",VERTEX,{"derivedFrom":[subQ17,subQ2]});Q25=makeQuery(id+"F2.imprint","IMPRINT",FACE,{"disambiguationData":[TD([[makeQuery(id+"F2.imprint","IMPRINT",EDGE,{"disambiguationData":[TD([[subQ18,1.0]])],"derivedFrom":subQ17}),1.0]])]});}
            extrude(context, id + "F3", {"entities" : qUnion([Q0, Q1, Q2, Q3, Q4, Q5, Q6, Q7, Q8, Q9, Q10, Q11, Q12, Q13, Q14, Q15, Q16, Q17, Q18, Q19, Q20, Q21, Q22, Q23, Q24, Q25]), "operationType" : NewBodyOperationType.ADD, "depth" : 1.27 * mm});
        }
        {
            var Q0;
            Q0=makeQuery(id+"F2.imprint","IMPRINT",FACE,{"disambiguationData":[TD([[makeQuery(id+"F2.imprint","IMPRINT",EDGE,{"derivedFrom":sQuery(id+"F2.wireOp",EDGE,"E127")}),1.0]])]});
            extrude(context, id + "F4", {"entities" : qUnion([Q0]), "operationType" : NewBodyOperationType.ADD, "depth" : 1.27 * mm});
        }
        {
            var Q0;
            {var subQ61=sQuery(id+"F0.wireOp",EDGE,"E8.MirrorCS");var subQ79=sQuery(id+"F0.wireOp",EDGE,"E6.MirrorCS");var subQ81=sQuery(id+"F0.wireOp",EDGE,"E5");var subQ91=sQuery(id+"F0.wireOp",EDGE,"E4");var subQ92=makeQuery(id+"F1.opExtrude","SWEPT_FACE",FACE,{"disambiguationData":[OSD([subQ91])]});Q0=makeQuery(id+"F4.boolean.opBoolean","SPLIT",FACE,{"disambiguationData":[TD([subQ92])],"derivedFrom":makeQuery(id+"F3.boolean.opBoolean","SPLIT",FACE,{"disambiguationData":[TD([subQ92])],"derivedFrom":makeQuery(id+"F1.opExtrude","CAP_FACE",FACE,{"disambiguationData":[OSD([subQ91,subQ81,subQ79,subQ61])],"isStart":false})})});}
            var sketch = newSketch(context, id + "F5", { "sketchPlane" : qUnion([Q0])});
            skText(sketch, "E226", { "text": "         UNCC\nFENCING CLUB", "fontName": "NotoSerif-Regular.ttf"});
            const initialGuessF5  = {"E226": [-0.0218, 0.0445, 1, 0, 0.00436]};
            skSetInitialGuess(sketch, initialGuessF5);
            skSolve(sketch);
        }
        {
            var Q0;
            {var subQ63=sQuery(id+"F0.wireOp",EDGE,"E8.MirrorCS");var subQ81=sQuery(id+"F0.wireOp",EDGE,"E6.MirrorCS");var subQ83=sQuery(id+"F0.wireOp",EDGE,"E5");var subQ93=sQuery(id+"F0.wireOp",EDGE,"E4");var subQ94=makeQuery(id+"F1.opExtrude","SWEPT_FACE",FACE,{"disambiguationData":[OSD([subQ93])]});Q0=makeQuery(id+"F4.boolean.opBoolean","SPLIT",FACE,{"disambiguationData":[TD([subQ94])],"derivedFrom":makeQuery(id+"F3.boolean.opBoolean","SPLIT",FACE,{"disambiguationData":[TD([subQ94])],"derivedFrom":makeQuery(id+"F1.opExtrude","CAP_FACE",FACE,{"disambiguationData":[OSD([subQ93,subQ83,subQ81,subQ63])],"isStart":false})})});}
            var sketch = newSketch(context, id + "F6", { "sketchPlane" : qUnion([Q0])});
            skText(sketch, "E227", { "text": "1", "fontName": "NotoSerif-Regular.ttf"});
            skText(sketch, "E228", { "text": "st", "fontName": "NotoSerif-Regular.ttf"});
            const initialGuessF6  = {"E227": [-0.00764, -0.04307, 1, 0, 0.01046], "E228": [-0.00071, -0.03906, 1, 0, 0.00645]};
            skSetInitialGuess(sketch, initialGuessF6);
            skSolve(sketch);
        }
        {
            var Q0;
            Q0=makeQuery(id+"F6.imprint","IMPRINT",FACE,{"disambiguationData":[TD([[makeQuery(id+"F6.imprint","IMPRINT",EDGE,{"derivedFrom":sQuery(id+"F6.wireOp",EDGE,"E227.sketch_text.stroke-0")}),1.0]])]});
            var sketch = newSketch(context, id + "F7", { "sketchPlane" : qUnion([Q0])});
            skText(sketch, "E229", { "text": "3", "fontName": "NotoSerif-Regular.ttf"});
            skText(sketch, "E230", { "text": "rd", "fontName": "NotoSerif-Regular.ttf"});
            const initialGuessF7  = {"E229": [-0.0077, -0.04265, 1, 0, 0.0105], "E230": [-0.0004, -0.03883, 1, 0, 0.0067]};
            skSetInitialGuess(sketch, initialGuessF7);
            skSolve(sketch);
        }
        {
            var Q0;
            Q0 = qSketchRegion(id + "F5", true);
            extrude(context, id + "F8", {"entities" : qUnion([Q0]), "operationType" : NewBodyOperationType.ADD, "depth" : 1.27 * mm});
        }
        {
            var Q0;
            {var subQ61=sQuery(id+"F7.wireOp",EDGE,"E229.sketch_text.stroke-8");Q0=makeQuery(id+"F7.imprint","IMPRINT",FACE,{"disambiguationData":[TD([[makeQuery(id+"F7.imprint","IMPRINT",EDGE,{"derivedFrom":subQ61}),1.0]])]});}
            var sketch = newSketch(context, id + "F9", { "sketchPlane" : qUnion([Q0])});
            skPoint(sketch, "E231", {"position": v(-26.4, 26.4) * mm});
            skPoint(sketch, "E232", {"position": v(26.73, 26.4) * mm});
            skSolve(sketch);
        }
        {
            var Q0;
            Q0=sQuery(id+"F9.wireOp",VERTEX,"E231");
            var Q1;
            Q1=sQuery(id+"F9.wireOp",VERTEX,"E232");
            var Q2;
            Q2=makeQuery(id+"F1.opExtrude","SWEPT_BODY",BODY,{"disambiguationData":[OSD([sQuery(id+"F0.wireOp",EDGE,"E4"),sQuery(id+"F0.wireOp",EDGE,"E5"),sQuery(id+"F0.wireOp",EDGE,"E6.MirrorCS"),sQuery(id+"F0.wireOp",EDGE,"E8.MirrorCS")])]});
            hole(context, id + "F10", {"style" : HoleStyle.SIMPLE, "endStyle" : HoleEndStyle.THROUGH, "holeDiameter" : 6.35 * mm, "locations" : qUnion([Q0, Q1]), "scope" : qUnion([Q2]), "isTappedThrough" : true});
        }
    });
